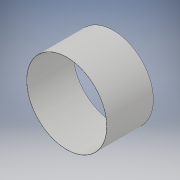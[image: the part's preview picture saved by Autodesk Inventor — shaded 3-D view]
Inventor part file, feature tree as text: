
AUTODESK INVENTOR PART (.ipt)
format: ipt  version: 2019 (Build 230136000, 136)  size: 103,936 bytes
history: native  units: mm
features: extrude x2, sketch x2
ambient origin geometry x8: Origin, YZ Plane, XZ Plane, XY Plane, X Axis, Y Axis, Z Axis, Center Point
bodies: Solid1 (feature_tree)
feature tree (4):
  extrude  "Extrusion1"  Depth=116.8mm TaperAngle=0.0deg
  extrude  "Extrusion2"  Depth=11.68mm TaperAngle=0.0deg
  sketch  "Sketch1"  dims[d0=201.7mm d1=116.8mm d2=0.0mm]
  sketch  "Sketch2"  dims[d3=200.7mm d4=11.68mm d5=0.0mm]
